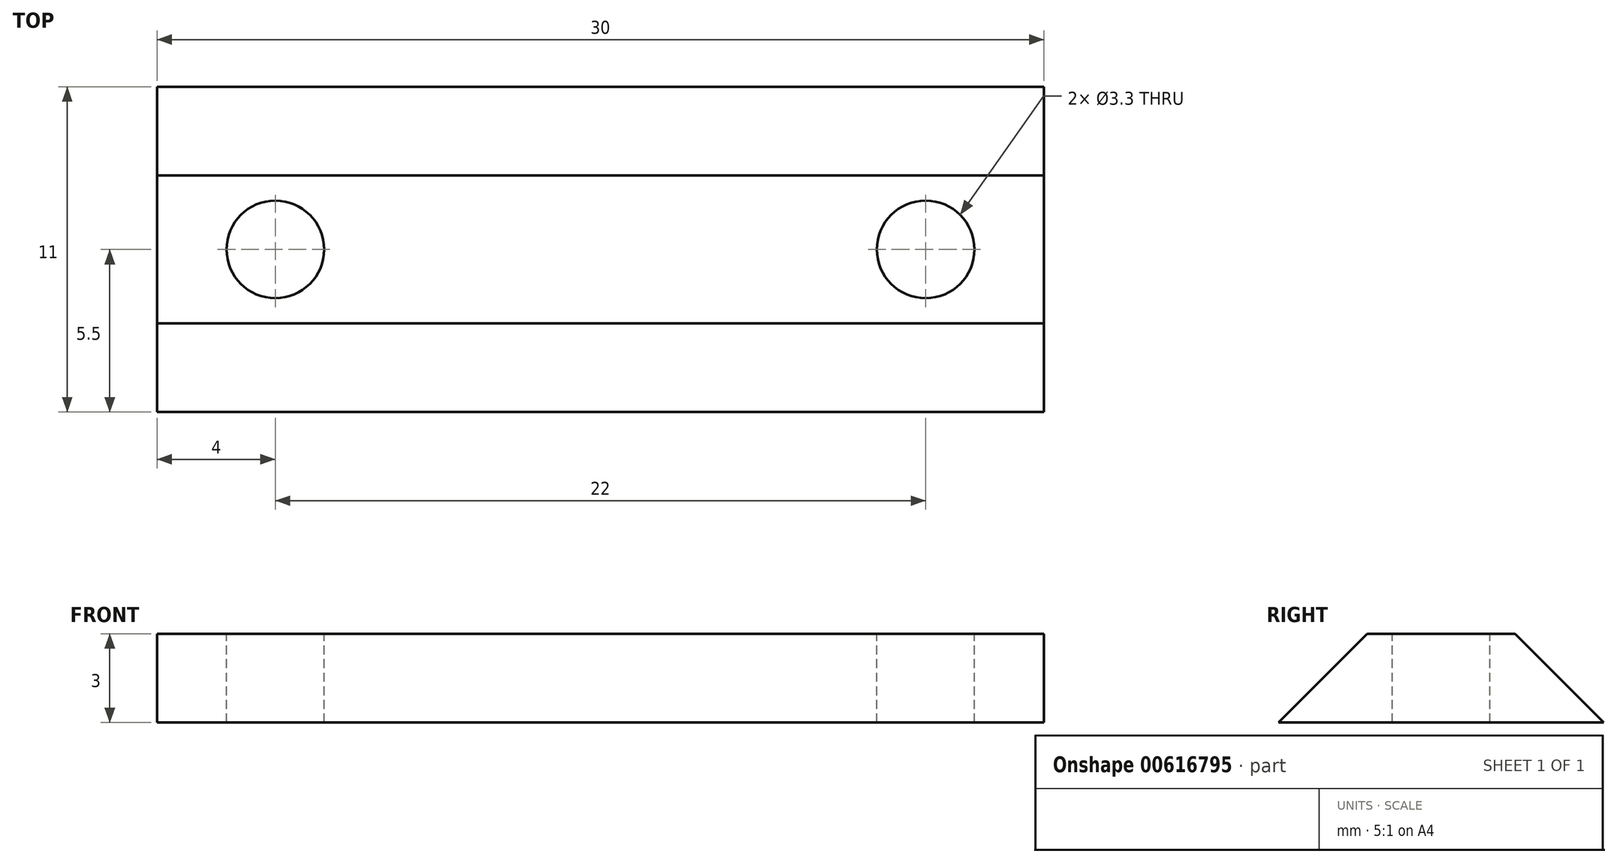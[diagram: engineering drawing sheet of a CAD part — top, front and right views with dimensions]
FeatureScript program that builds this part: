
annotation { "Feature Type Name" : "Feature", "Feature Type Description" : "" }
export const myFeature = defineFeature(function(context is Context, id is Id, definition is map)
    precondition{}
    {
        {
            var Q0;
            Q0=qCreatedBy(makeId("Top.planeOp"),FACE);
            var sketch = newSketch(context, id + "F0", { "sketchPlane" : qUnion([Q0])});
            skLineSegment(sketch, "E0.bottom", {"start": v(0, 0) * mm, "end": v(30, 0) * mm});
            skLineSegment(sketch, "E0.top", {"start": v(0, -11) * mm, "end": v(30, -11) * mm});
            skLineSegment(sketch, "E0.left", {"start": v(0, 0) * mm, "end": v(0, -11) * mm});
            skLineSegment(sketch, "E0.right", {"start": v(30, 0) * mm, "end": v(30, -11) * mm});
            skPoint(sketch, "E1", {"position": v(4, -5.5) * mm});
            skPoint(sketch, "E1.positionSnap0", {"position": v(0, -5.5) * mm});
            skPoint(sketch, "E2", {"position": v(26, -5.5) * mm});
            skLineSegment(sketch, "E3", {"start": v(15, 0) * mm, "end": v(15, -11) * mm, "construction": true});
            skSolve(sketch);
        }
        {
            var Q0;
            Q0 = qSketchRegion(id + "F0", true);
            extrude(context, id + "F1", {"entities" : qUnion([Q0]), "depth" : 3 * mm, "offsetDistance" : 25 * mm});
        }
        {
            var Q0;
            Q0=makeQuery(id+"F1.opExtrude","CAP_EDGE",EDGE,{"disambiguationData":[OSD([sQuery(id+"F0.wireOp",EDGE,"E0.top")])],"isStart":false});
            var Q1;
            Q1=makeQuery(id+"F1.opExtrude","CAP_EDGE",EDGE,{"disambiguationData":[OSD([sQuery(id+"F0.wireOp",EDGE,"E0.bottom")])],"isStart":false});
            chamfer(context, id + "F2", {"entities" : qUnion([Q0, Q1]), "chamferType" : ChamferType.OFFSET_ANGLE, "width" : 3 * mm, "oppositeDirection" : false, "angle" : 45 * degree, "tangentPropagation" : true});
        }
        {
            var Q0;
            Q0=sQuery(id+"F0.wireOp",VERTEX,"E1");
            var Q1;
            Q1=sQuery(id+"F0.wireOp",VERTEX,"E2");
            var Q2;
            Q2=makeQuery(id+"F1.opExtrude","SWEPT_BODY",BODY,{"disambiguationData":[OSD([sQuery(id+"F0.wireOp",EDGE,"E0.bottom"),sQuery(id+"F0.wireOp",EDGE,"E0.top"),sQuery(id+"F0.wireOp",EDGE,"E0.left"),sQuery(id+"F0.wireOp",EDGE,"E0.right")])]});
            hole(context, id + "F3", {"style" : HoleStyle.SIMPLE, "endStyle" : HoleEndStyle.THROUGH, "oppositeDirection" : true, "standardTappedOrClearance" : lookupTablePath({ "standard" : "ISO", "engagement" : "75%", "pitch" : "0.7 mm", "size" : "M4", "type" : "Tapped" }), "standardBlindInLast" : lookupTablePath({ "standard" : "ISO", "fit" : "Normal", "engagement" : "75%", "pitch" : "0.7 mm", "size" : "M4", "type" : "Clearance & tapped" }), "holeDiameter" : 3.3 * mm, "majorDiameter" : 4 * mm, "showTappedDepth" : true, "isTappedThrough" : true, "tappedDepth" : 12 * mm, "tapClearance" : 3, "locations" : qUnion([Q0, Q1]), "scope" : qUnion([Q2]), "startStyle" : HoleStartStyle.PART});
        }
    });
